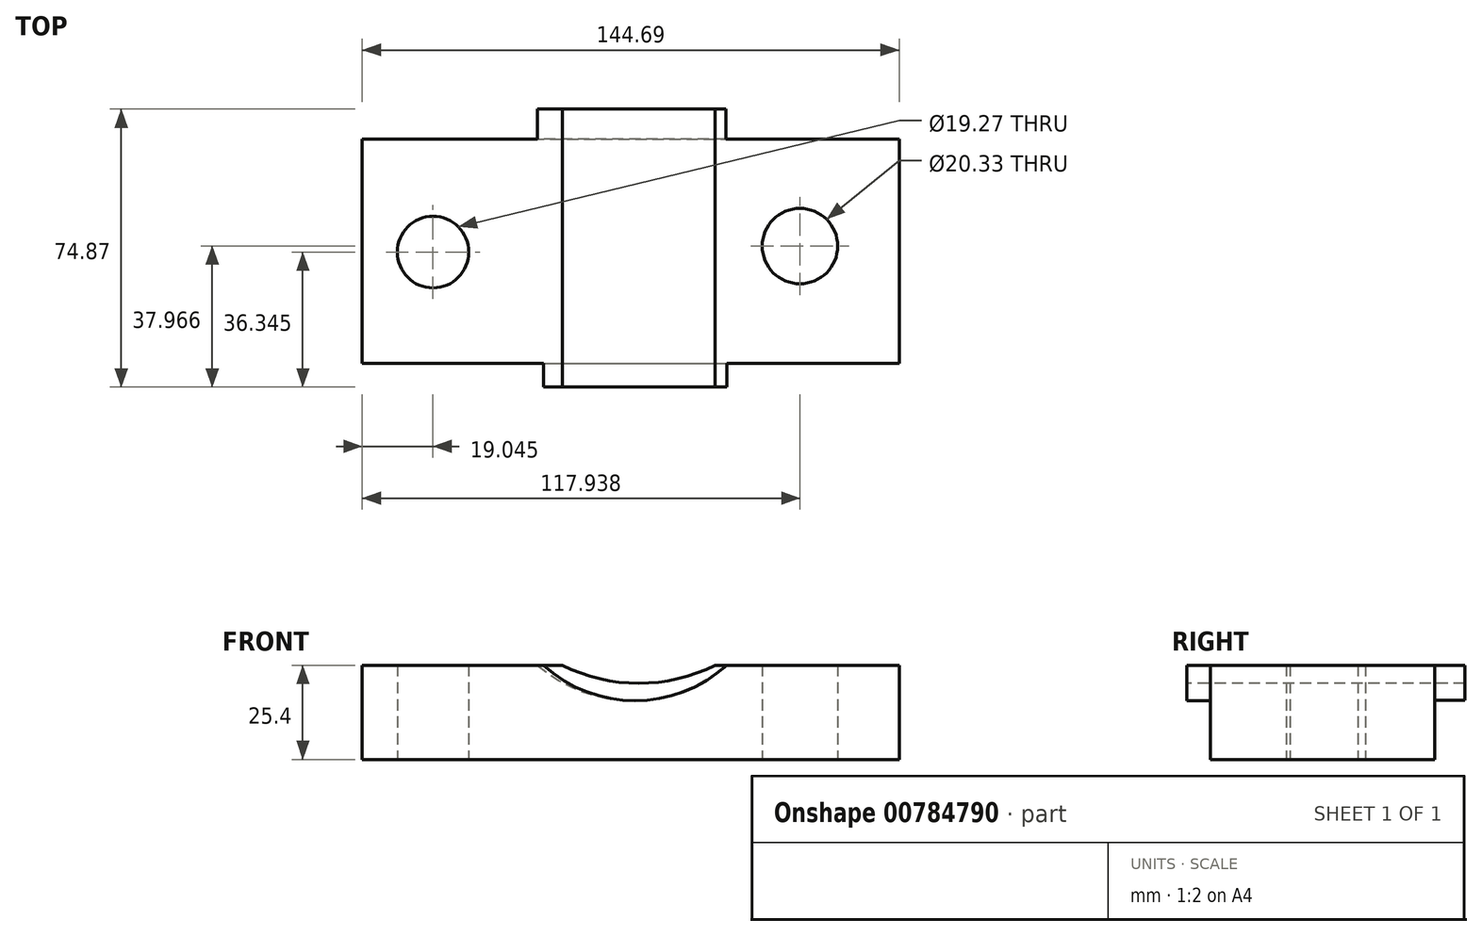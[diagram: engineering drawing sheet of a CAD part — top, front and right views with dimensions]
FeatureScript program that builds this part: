
annotation { "Feature Type Name" : "Feature", "Feature Type Description" : "" }
export const myFeature = defineFeature(function(context is Context, id is Id, definition is map)
    precondition{}
    {
        {
            var Q0;
            Q0=qCreatedBy(makeId("Top.planeOp"),FACE);
            var sketch = newSketch(context, id + "F0", { "sketchPlane" : qUnion([Q0])});
            skLineSegment(sketch, "E0.bottom", {"start": v(-71.35, 20.27) * mm, "end": v(73.34, 20.27) * mm});
            skLineSegment(sketch, "E0.top", {"start": v(-71.35, -40.12) * mm, "end": v(73.34, -40.12) * mm});
            skLineSegment(sketch, "E0.left", {"start": v(-71.35, 20.27) * mm, "end": v(-71.35, -40.12) * mm});
            skLineSegment(sketch, "E0.right", {"start": v(73.34, 20.27) * mm, "end": v(73.34, -40.12) * mm});
            skCircle(sketch, "E1", {"center": v(-52.3, -10.12) * mm, "radius": 9.63 * mm});
            skCircle(sketch, "E2", {"center": v(46.59, -8.5) * mm, "radius": 10.16 * mm});
            skSolve(sketch);
        }
        {
            var Q0;
            Q0=makeQuery(id+"F0.imprint","IMPRINT",FACE,{"disambiguationData":[TD([[makeQuery(id+"F0.imprint","IMPRINT",EDGE,{"derivedFrom":sQuery(id+"F0.wireOp",EDGE,"E0.bottom")}),-1.0]])]});
            extrude(context, id + "F1", {"entities" : qUnion([Q0]), "depth" : 25.4 * mm, "offsetDistance" : 25.4 * mm});
        }
        {
            var Q0;
            Q0=makeQuery(id+"F1.opExtrude","SWEPT_FACE",FACE,{"disambiguationData":[OSD([sQuery(id+"F0.wireOp",EDGE,"E0.top")])]});
            var sketch = newSketch(context, id + "F2", { "sketchPlane" : qUnion([Q0])});
            skArc(sketch, "E3", {"start": v(-17.44, 25.4) * mm, "mid": v(3.15, 20.5) * mm, "end": v(23.74, 25.4) * mm});
            skArc(sketch, "E4", {"start": v(-22.5, 25.4) * mm, "mid": v(2.17, 15.82) * mm, "end": v(26.83, 25.4) * mm});
            skLineSegment(sketch, "E5", {"start": v(-17.44, 25.4) * mm, "end": v(23.74, 25.4) * mm});
            skLineSegment(sketch, "E6", {"start": v(-22.5, 25.4) * mm, "end": v(-17.44, 25.4) * mm});
            skLineSegment(sketch, "E7", {"start": v(23.74, 25.4) * mm, "end": v(26.83, 25.4) * mm});
            skSolve(sketch);
        }
        {
            var Q0;
            Q0=makeQuery(id+"F2.imprint","IMPRINT",FACE,{"disambiguationData":[TD([[makeQuery(id+"F2.imprint","IMPRINT",EDGE,{"derivedFrom":sQuery(id+"F2.wireOp",EDGE,"E3")}),1.0]])]});
            extrude(context, id + "F3", {"entities" : qUnion([Q0]), "operationType" : NewBodyOperationType.REMOVE, "oppositeDirection" : true, "depth" : 61.2 * mm, "offsetDistance" : 25.4 * mm});
        }
        {
            var Q0;
            Q0=makeQuery(id+"F2.imprint","IMPRINT",FACE,{"disambiguationData":[TD([[makeQuery(id+"F2.imprint","IMPRINT",EDGE,{"derivedFrom":sQuery(id+"F2.wireOp",EDGE,"E3")}),-1.0]])]});
            extrude(context, id + "F4", {"entities" : qUnion([Q0]), "operationType" : NewBodyOperationType.ADD, "depth" : 6.35 * mm, "offsetDistance" : 25.4 * mm});
        }
        {
            var Q0;
            Q0=makeQuery(id+"F1.opExtrude","SWEPT_FACE",FACE,{"disambiguationData":[OSD([sQuery(id+"F0.wireOp",EDGE,"E0.bottom")])]});
            var sketch = newSketch(context, id + "F5", { "sketchPlane" : qUnion([Q0])});
            skArc(sketch, "E8", {"start": v(-26.6, 25.4) * mm, "mid": v(-1.23, 15.9) * mm, "end": v(24.15, 25.4) * mm});
            skSolve(sketch);
        }
        {
            var Q0;
            {var subQ0=sQuery(id+"F5.wireOp",EDGE,"E8");Q0=makeQuery(id+"F5.imprint","IMPRINT",FACE,{"disambiguationData":[TD([[makeQuery(id+"F5.imprint","IMPRINT",EDGE,{"derivedFrom":subQ0}),1.0]])]});}
            extrude(context, id + "F6", {"entities" : qUnion([Q0]), "operationType" : NewBodyOperationType.ADD, "depth" : 8.13 * mm, "offsetDistance" : 25.4 * mm});
        }
    });
